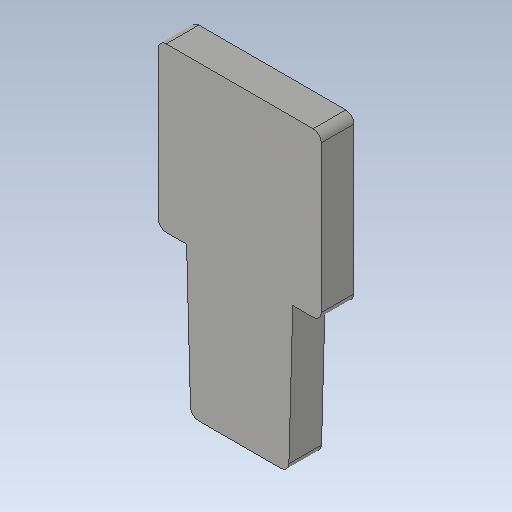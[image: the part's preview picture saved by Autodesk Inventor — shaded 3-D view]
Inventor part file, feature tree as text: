
AUTODESK INVENTOR PART (.ipt)
format: ipt  version: 2020.1 (Build 241239000, 239)  size: 145,408 bytes
history: native  units: mm
features: other x2, sheet_metal_op x1, sketch x1
ambient origin geometry x8: Origin, YZ Plane, XZ Plane, XY Plane, X Axis, Y Axis, Z Axis, Center Point
bodies: Solid1 (feature_tree)
feature tree (4):
  sheet_metal_op  "Face1"
  sketch  "Sketch1"  dims[d0=24.0mm d1=26.0mm d2=40.0mm d3=36.0mm d4=40.0mm d5=2.0mm d6=8.0mm]
  other  "Plate1"
  other  "Definition1"
